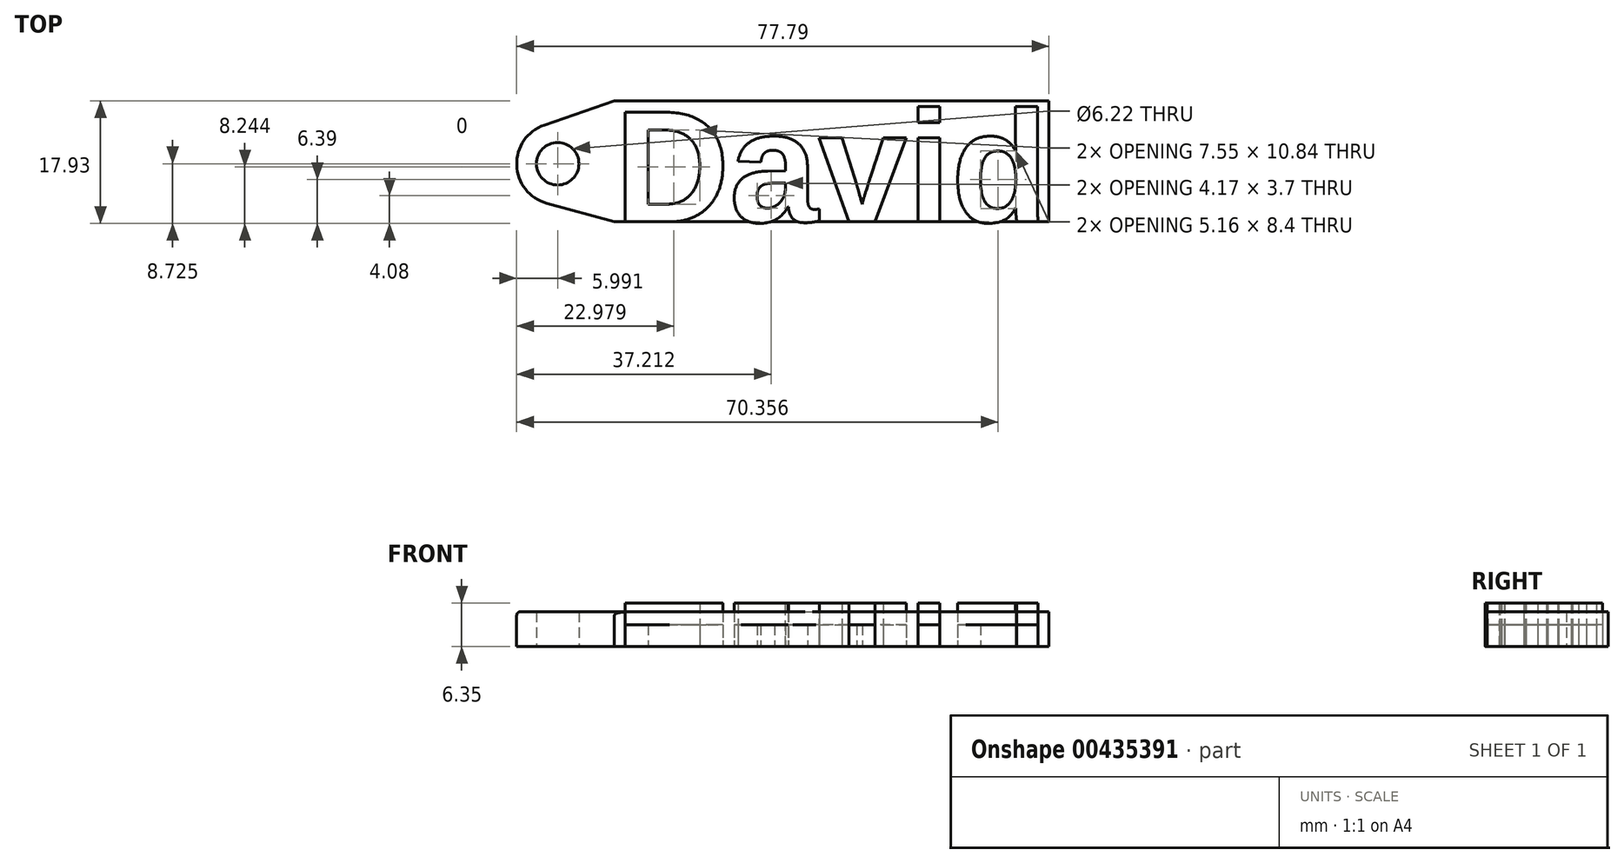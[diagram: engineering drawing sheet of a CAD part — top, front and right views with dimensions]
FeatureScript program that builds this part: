
annotation { "Feature Type Name" : "Feature", "Feature Type Description" : "" }
export const myFeature = defineFeature(function(context is Context, id is Id, definition is map)
    precondition{}
    {
        {
            var Q0;
            Q0=qCreatedBy(makeId("Top.planeOp"),FACE);
            var sketch = newSketch(context, id + "F0", { "sketchPlane" : qUnion([Q0])});
            skText(sketch, "E0", { "text": "David", "fontName": "Arimo-Bold.ttf"});
            const initialGuessF0  = {"E0": [0, 0, 1, 0, 0.01677]};
            skSetInitialGuess(sketch, initialGuessF0);
            skSolve(sketch);
        }
        {
            var Q0;
            Q0 = qSketchRegion(id + "F0", true);
            extrude(context, id + "F1", {"entities" : qUnion([Q0]), "depth" : 3.17 * mm});
        }
        {
            var Q0;
            Q0 = qSketchRegion(id + "F0", true);
            extrude(context, id + "F2", {"entities" : qUnion([Q0]), "depth" : 6.35 * mm});
        }
        {
            var Q0;
            Q0=qCreatedBy(makeId("Top.planeOp"),FACE);
            var sketch = newSketch(context, id + "F3", { "sketchPlane" : qUnion([Q0])});
            skLineSegment(sketch, "E1.bottom", {"start": v(0, 0) * mm, "end": v(63.5, 0) * mm});
            skLineSegment(sketch, "E1.top", {"start": v(0, 17.7) * mm, "end": v(63.5, 17.7) * mm});
            skLineSegment(sketch, "E1.left", {"start": v(0, 0) * mm, "end": v(0, 17.7) * mm});
            skLineSegment(sketch, "E1.right", {"start": v(63.5, 0) * mm, "end": v(63.5, 17.7) * mm});
            skSolve(sketch);
        }
        {
            var Q0;
            Q0=makeQuery(id+"F3.imprint","IMPRINT",FACE,{"disambiguationData":[TD([[makeQuery(id+"F3.imprint","IMPRINT",EDGE,{"derivedFrom":sQuery(id+"F3.wireOp",EDGE,"E1.bottom")}),1.0]])]});
            extrude(context, id + "F4", {"entities" : qUnion([Q0]), "depth" : 5.08 * mm});
        }
        {
            var Q0;
            Q0=qCreatedBy(makeId("Top.planeOp"),FACE);
            var sketch = newSketch(context, id + "F5", { "sketchPlane" : qUnion([Q0])});
            skCircle(sketch, "E2", {"center": v(-8.3, 8.5) * mm, "radius": 5.99 * mm});
            skCircle(sketch, "E3", {"center": v(-8.3, 8.5) * mm, "radius": 3.1 * mm});
            skSolve(sketch);
        }
        {
            var Q0;
            Q0=makeQuery(id+"F5.imprint","IMPRINT",FACE,{"disambiguationData":[TD([[makeQuery(id+"F5.imprint","IMPRINT",EDGE,{"derivedFrom":sQuery(id+"F5.wireOp",EDGE,"E3")}),1.0]])]});
            var sketch = newSketch(context, id + "F6", { "sketchPlane" : qUnion([Q0])});
            skCircle(sketch, "E4.0", {"center": v(-8.3, 8.5) * mm, "radius": 3.1 * mm});
            skCircle(sketch, "E5.0", {"center": v(-8.3, 8.5) * mm, "radius": 5.99 * mm});
            skLineSegment(sketch, "E6", {"start": v(-10.25, 14.15) * mm, "end": v(0, 17.7) * mm});
            skLineSegment(sketch, "E7", {"start": v(-9.89, 2.72) * mm, "end": v(0, 0) * mm});
            skLineSegment(sketch, "E8", {"start": v(0, 17.7) * mm, "end": v(0, 0) * mm});
            skSolve(sketch);
        }
        {
            var Q0;
            Q0=makeQuery(id+"F5.imprint","IMPRINT",FACE,{"disambiguationData":[TD([[makeQuery(id+"F5.imprint","IMPRINT",EDGE,{"derivedFrom":sQuery(id+"F5.wireOp",EDGE,"E2")}),1.0]])]});
            var Q1;
            {var subQ0=sQuery(id+"F6.wireOp",EDGE,"E6");Q1=makeQuery(id+"F6.imprint","IMPRINT",FACE,{"disambiguationData":[TD([[makeQuery(id+"F6.imprint","IMPRINT",EDGE,{"derivedFrom":subQ0}),-1.0]])]});}
            var Q2;
            Q2=makeQuery(id+"F4.opExtrude","CAP_FACE",FACE,{"disambiguationData":[OSD([sQuery(id+"F3.wireOp",EDGE,"E1.bottom"),sQuery(id+"F3.wireOp",EDGE,"E1.top"),sQuery(id+"F3.wireOp",EDGE,"E1.left"),sQuery(id+"F3.wireOp",EDGE,"E1.right")])],"isStart":false});
            extrude(context, id + "F7", {"entities" : qUnion([Q0, Q1]), "operationType" : NewBodyOperationType.ADD, "endBound" : BoundingType.UP_TO_SURFACE, "endBoundEntityFace" : qUnion([Q2]), "depth" : 25.4 * mm});
        }
        {
            var Q0;
            Q0=makeQuery(id+"F7.opExtrude","CAP_EDGE",EDGE,{"disambiguationData":[OSD([sQuery(id+"F6.wireOp",EDGE,"E6")])],"isStart":false});
            var Q1;
            Q1=makeQuery(id+"F7.opExtrude","CAP_EDGE",EDGE,{"disambiguationData":[OSD([sQuery(id+"F6.wireOp",EDGE,"E7")])],"isStart":false});
            fillet(context, id + "F8", {"entities" : qUnion([Q0, Q1]), "radius" : 0.5 * mm, "tangentPropagation" : true, "allowEdgeOverflow" : false});
        }
    });
